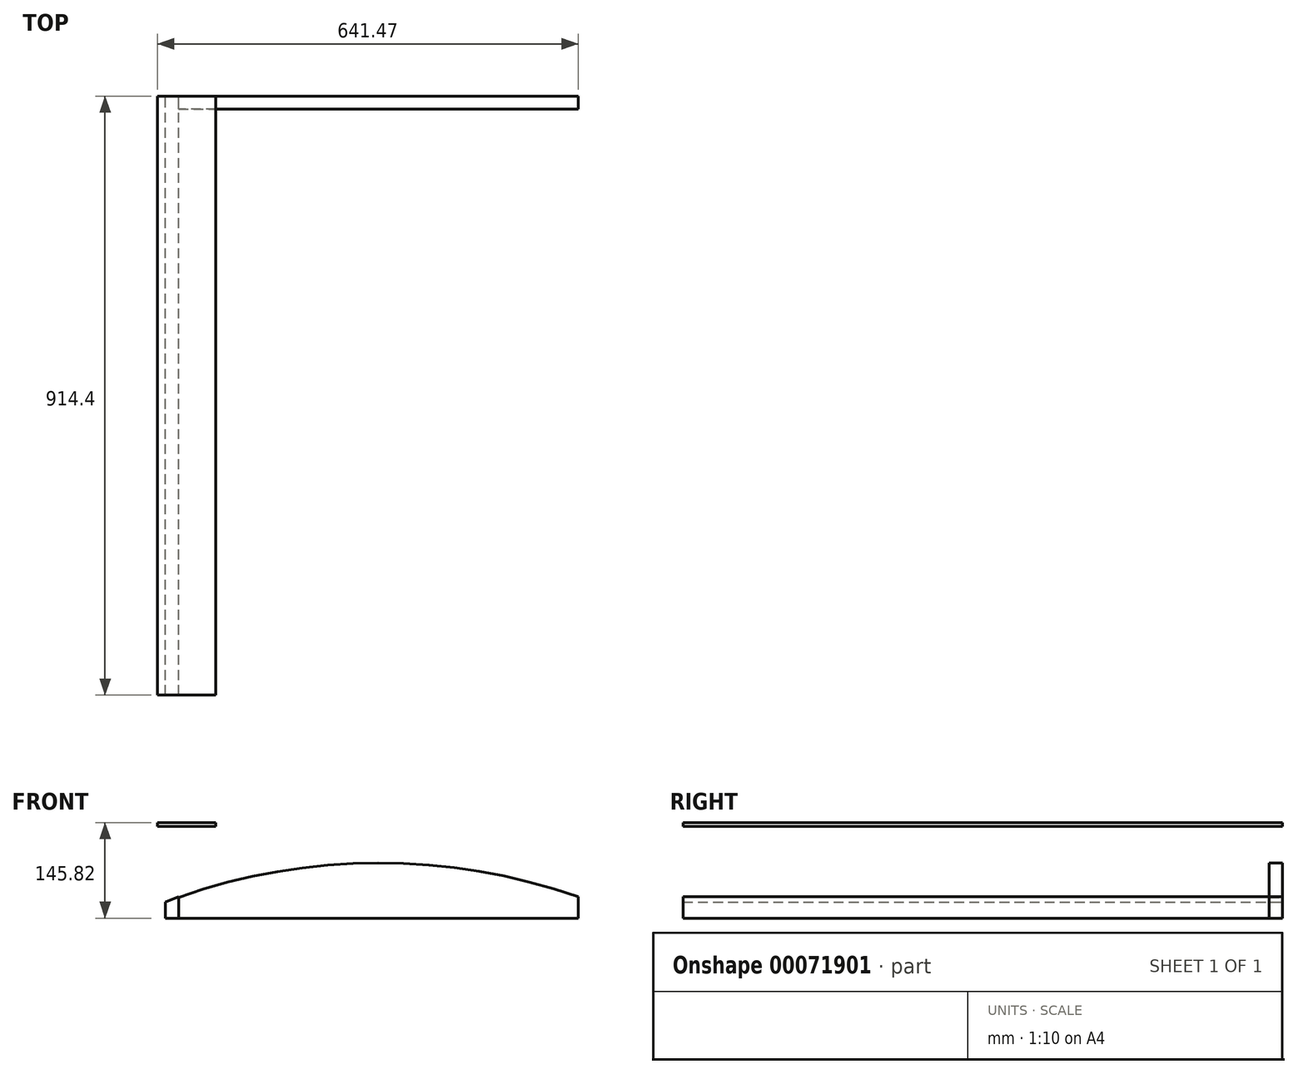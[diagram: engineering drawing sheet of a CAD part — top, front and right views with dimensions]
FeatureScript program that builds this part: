
annotation { "Feature Type Name" : "Feature", "Feature Type Description" : "" }
export const myFeature = defineFeature(function(context is Context, id is Id, definition is map)
    precondition{}
    {
        {
            var Q0;
            Q0=qCreatedBy(makeId("Front.planeOp"),FACE);
            var sketch = newSketch(context, id + "F0", { "sketchPlane" : qUnion([Q0])});
            skLineSegment(sketch, "E0", {"start": v(0, 0) * mm, "end": v(609.6, 0) * mm});
            skLineSegment(sketch, "E1", {"start": v(0, 0) * mm, "end": v(0, 31.74) * mm});
            skLineSegment(sketch, "E2", {"start": v(609.6, 0) * mm, "end": v(609.6, 32.5) * mm});
            skArc(sketch, "E3", {"start": v(609.6, 32.5) * mm, "mid": v(304.73, 84.37) * mm, "end": v(0, 31.74) * mm});
            skSolve(sketch);
        }
        {
            var Q0;
            Q0 = qSketchRegion(id + "F0", true);
            extrude(context, id + "F1", {"entities" : qUnion([Q0]), "depth" : 20 * mm, "offsetDistance" : 25 * mm});
        }
        {
            var Q0;
            Q0=qCreatedBy(makeId("Front.planeOp"),FACE);
            var sketch = newSketch(context, id + "F2", { "sketchPlane" : qUnion([Q0])});
            skLineSegment(sketch, "E4.bottom", {"start": v(-31.87, 145.82) * mm, "end": v(57.03, 145.82) * mm});
            skLineSegment(sketch, "E4.top", {"start": v(-31.87, 139.82) * mm, "end": v(57.03, 139.82) * mm});
            skLineSegment(sketch, "E4.left", {"start": v(-31.87, 145.82) * mm, "end": v(-31.87, 139.82) * mm});
            skLineSegment(sketch, "E4.right", {"start": v(57.03, 145.82) * mm, "end": v(57.03, 139.82) * mm});
            skSolve(sketch);
        }
        {
            var Q0;
            Q0 = qSketchRegion(id + "F2", true);
            extrude(context, id + "F3", {"entities" : qUnion([Q0]), "depth" : 914.4 * mm, "offsetDistance" : 25 * mm});
        }
        {
            var Q0;
            Q0=qCreatedBy(makeId("Front.planeOp"),FACE);
            var sketch = newSketch(context, id + "F4", { "sketchPlane" : qUnion([Q0])});
            skLineSegment(sketch, "E5", {"start": v(0, 0) * mm, "end": v(0, 32.51) * mm});
            skLineSegment(sketch, "E6", {"start": v(0, 0) * mm, "end": v(-20, 0) * mm});
            skLineSegment(sketch, "E7", {"start": v(-20, 0) * mm, "end": v(-20, 24.25) * mm});
            skLineSegment(sketch, "E8", {"start": v(-20, 24.25) * mm, "end": v(0, 32.51) * mm});
            skSolve(sketch);
        }
        {
            var Q0;
            Q0 = qSketchRegion(id + "F4", true);
            extrude(context, id + "F5", {"entities" : qUnion([Q0]), "depth" : 914.4 * mm, "offsetDistance" : 25 * mm});
        }
    });
